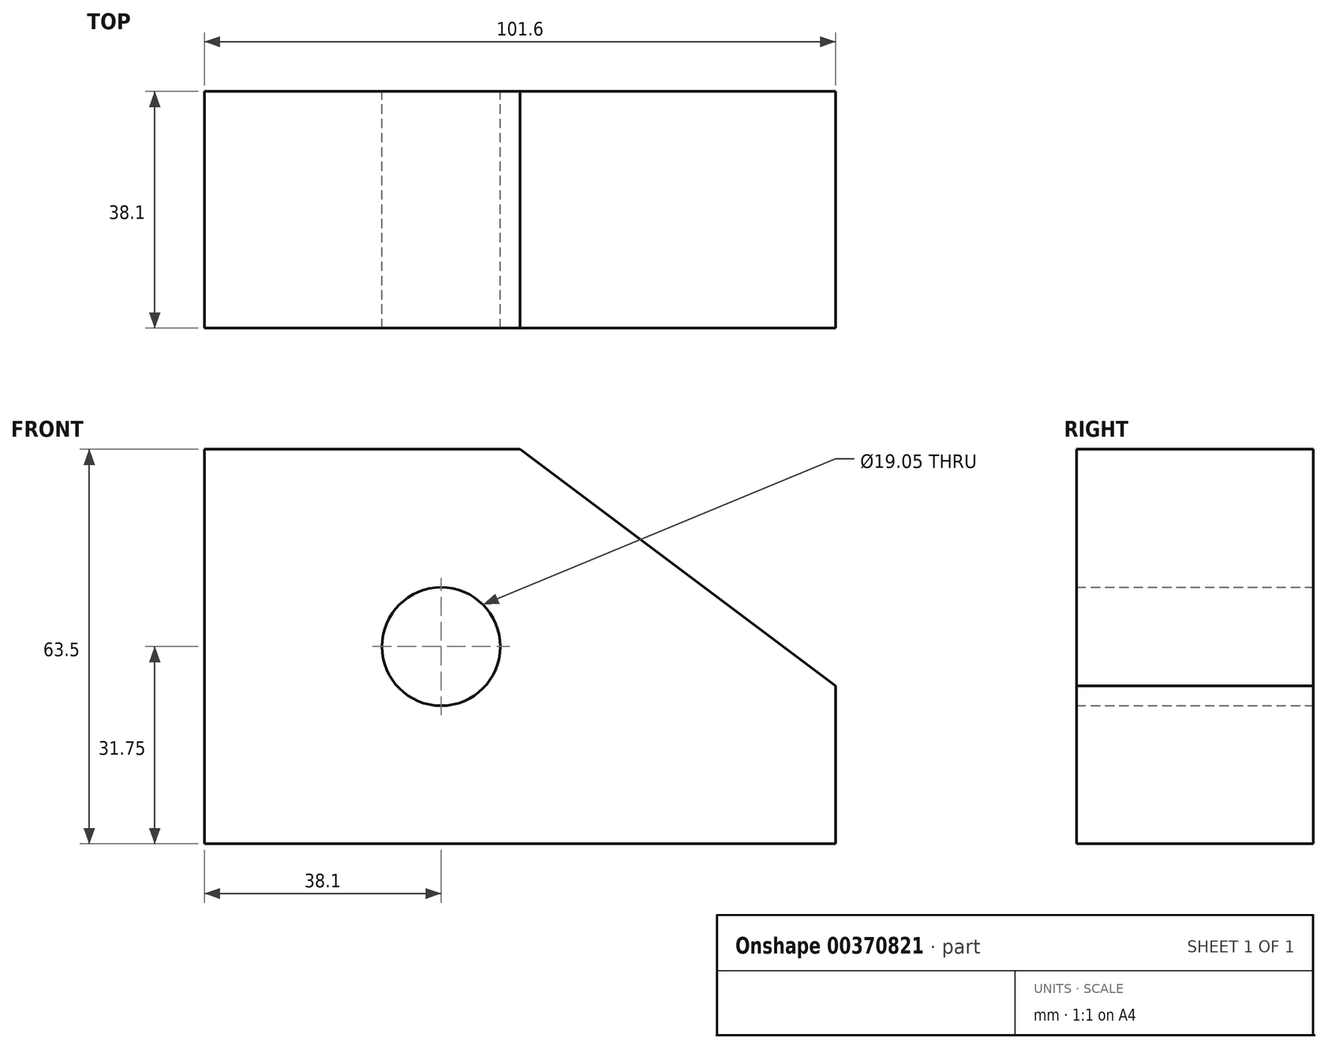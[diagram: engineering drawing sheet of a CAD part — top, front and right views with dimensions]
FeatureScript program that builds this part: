
annotation { "Feature Type Name" : "Feature", "Feature Type Description" : "" }
export const myFeature = defineFeature(function(context is Context, id is Id, definition is map)
    precondition{}
    {
        {
            var Q0;
            Q0=qCreatedBy(makeId("Front.planeOp"),FACE);
            var sketch = newSketch(context, id + "F0", { "sketchPlane" : qUnion([Q0])});
            skLineSegment(sketch, "E0", {"start": v(0, 0) * mm, "end": v(50.8, 0) * mm});
            skLineSegment(sketch, "E1", {"start": v(50.8, 0) * mm, "end": v(101.6, -38.1) * mm});
            skLineSegment(sketch, "E2", {"start": v(101.6, -38.1) * mm, "end": v(101.6, -63.5) * mm});
            skLineSegment(sketch, "E3", {"start": v(101.6, -63.5) * mm, "end": v(0, -63.5) * mm});
            skLineSegment(sketch, "E4", {"start": v(0, -63.5) * mm, "end": v(0, 0) * mm});
            skCircle(sketch, "E5", {"center": v(38.1, -31.75) * mm, "radius": 9.53 * mm});
            skSolve(sketch);
        }
        {
            var Q0;
            Q0 = qSketchRegion(id + "F0", true);
            extrude(context, id + "F1", {"entities" : qUnion([Q0]), "depth" : 38.1 * mm});
        }
    });
